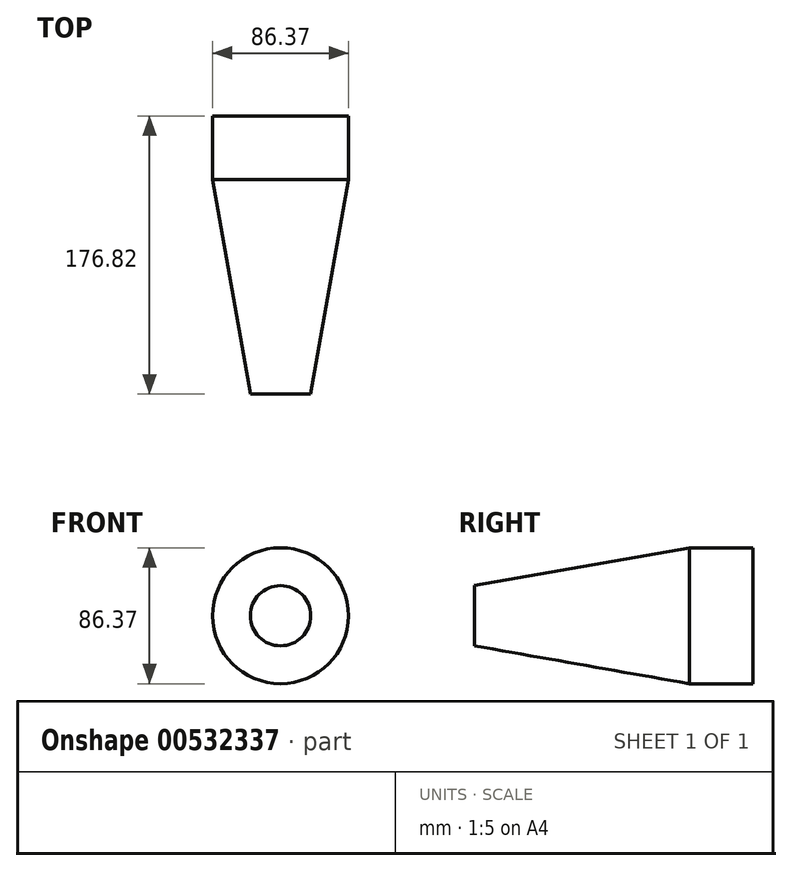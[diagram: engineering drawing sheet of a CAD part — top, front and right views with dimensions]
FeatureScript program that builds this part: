
annotation { "Feature Type Name" : "Feature", "Feature Type Description" : "" }
export const myFeature = defineFeature(function(context is Context, id is Id, definition is map)
    precondition{}
    {
        {
            var Q0;
            Q0=qCreatedBy(makeId("Front.planeOp"),FACE);
            var sketch = newSketch(context, id + "F0", { "sketchPlane" : qUnion([Q0])});
            skCircle(sketch, "E0", {"center": v(-10.84, 28.33) * mm, "radius": 43.19 * mm});
            skSolve(sketch);
        }
        {
            var Q0;
            Q0 = qSketchRegion(id + "F0", true);
            extrude(context, id + "F1", {"entities" : qUnion([Q0]), "depth" : 136.4 * mm, "offsetDistance" : 25.4 * mm, "hasDraft" : true, "draftAngle" : 10 * degree, "draftPullDirection" : true, "hasSecondDirection" : true, "secondDirectionOppositeDirection" : true, "secondDirectionDepth" : 40.42 * mm});
        }
    });
